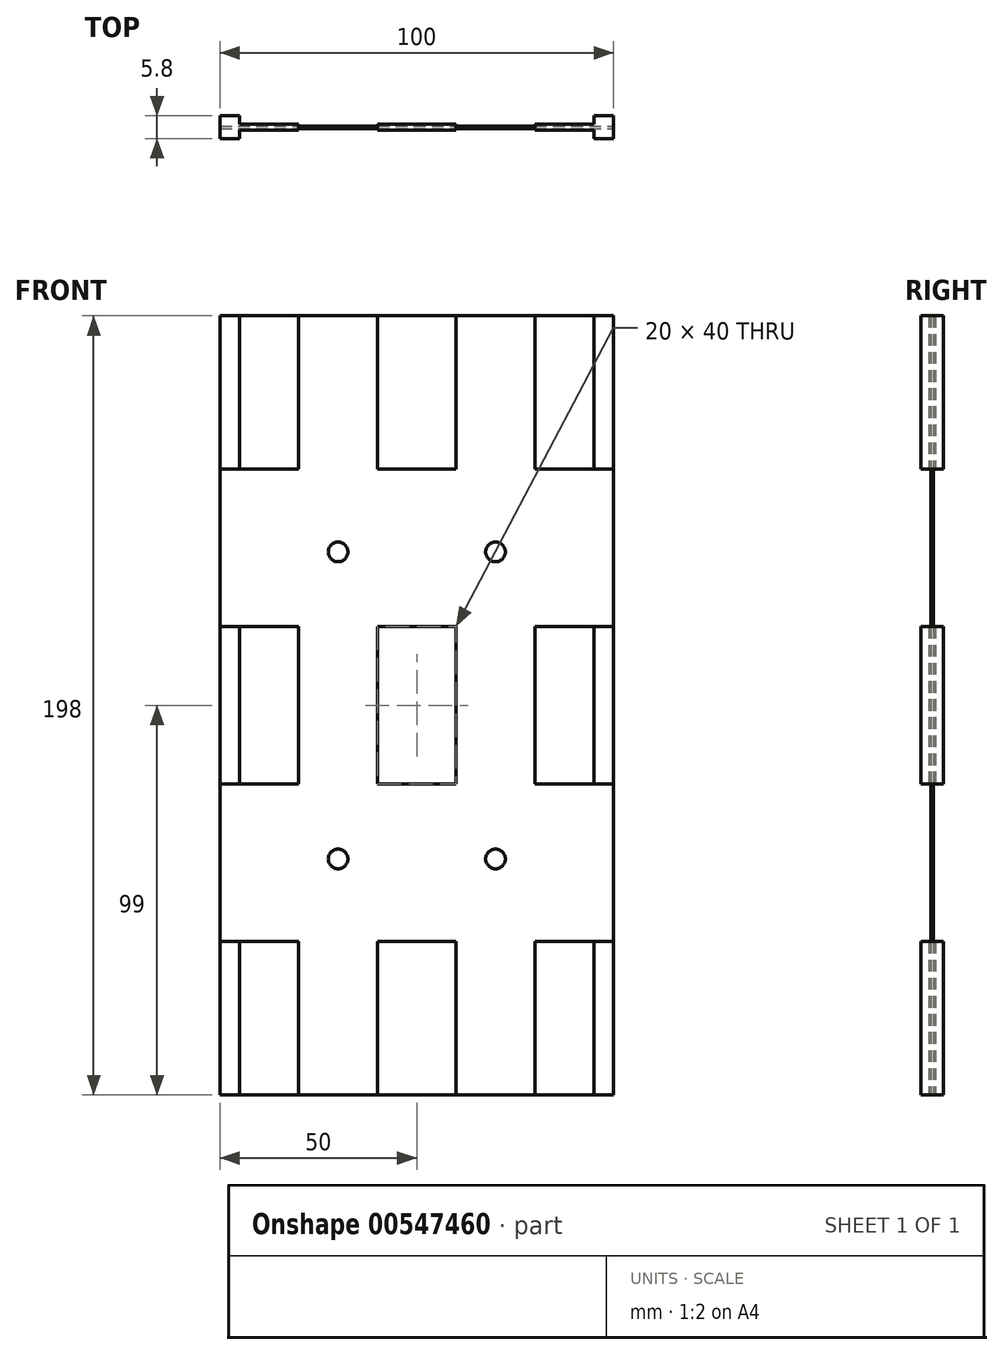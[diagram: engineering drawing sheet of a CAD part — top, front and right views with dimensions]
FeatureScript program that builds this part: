
annotation { "Feature Type Name" : "Feature", "Feature Type Description" : "" }
export const myFeature = defineFeature(function(context is Context, id is Id, definition is map)
    precondition{}
    {
        {
            var Q0;
            Q0=qCreatedBy(makeId("Front.planeOp"),FACE);
            var sketch = newSketch(context, id + "F0", { "sketchPlane" : qUnion([Q0])});
            skLineSegment(sketch, "E0.bottom", {"start": v(50, -99) * mm, "end": v(-50, -99) * mm});
            skLineSegment(sketch, "E0.top", {"start": v(50, 99) * mm, "end": v(-50, 99) * mm});
            skLineSegment(sketch, "E0.left", {"start": v(50, -99) * mm, "end": v(50, 99) * mm});
            skLineSegment(sketch, "E0.right", {"start": v(-50, -99) * mm, "end": v(-50, 99) * mm});
            skPoint(sketch, "E0.middle", {"position": v(0, 0) * mm});
            skLineSegment(sketch, "E1", {"start": v(45, 99) * mm, "end": v(45, -99) * mm});
            skLineSegment(sketch, "E2", {"start": v(30, 99) * mm, "end": v(30, -99) * mm});
            skLineSegment(sketch, "E3", {"start": v(10, 99) * mm, "end": v(10, -99) * mm});
            skLineSegment(sketch, "E4", {"start": v(-10, 99) * mm, "end": v(-10, -99) * mm});
            skLineSegment(sketch, "E5", {"start": v(-30, 99) * mm, "end": v(-30, -99) * mm});
            skLineSegment(sketch, "E6", {"start": v(-45, 99) * mm, "end": v(-45, -99) * mm});
            skLineSegment(sketch, "E7", {"start": v(-50, 60) * mm, "end": v(50, 60) * mm});
            skLineSegment(sketch, "E8", {"start": v(-50, 20) * mm, "end": v(50, 20) * mm});
            skLineSegment(sketch, "E9", {"start": v(-50, -20) * mm, "end": v(50, -20) * mm});
            skLineSegment(sketch, "E10", {"start": v(-50, -60) * mm, "end": v(50, -60) * mm});
            skSolve(sketch);
        }
        {
            var Q0;
            {var subQ0=sQuery(id+"F0.wireOp",EDGE,"E0.right");var subQ1=sQuery(id+"F0.wireOp",EDGE,"E0.bottom");var subQ2=makeQuery(id+"F0.imprint","INTERSECT",VERTEX,{"derivedFrom":[subQ1,subQ0]});Q0=makeQuery(id+"F0.imprint","IMPRINT",FACE,{"disambiguationData":[TD([[makeQuery(id+"F0.imprint","IMPRINT",EDGE,{"disambiguationData":[TD([[subQ2,1.0]])],"derivedFrom":subQ1}),-1.0]])]});}
            var Q1;
            {var subQ0=sQuery(id+"F0.wireOp",EDGE,"E0.right");var subQ1=sQuery(id+"F0.wireOp",EDGE,"E0.top");var subQ2=makeQuery(id+"F0.imprint","INTERSECT",VERTEX,{"derivedFrom":[subQ1,subQ0]});Q1=makeQuery(id+"F0.imprint","IMPRINT",FACE,{"disambiguationData":[TD([[makeQuery(id+"F0.imprint","IMPRINT",EDGE,{"disambiguationData":[TD([[subQ2,1.0]])],"derivedFrom":subQ1}),1.0]])]});}
            var Q2;
            {var subQ0=sQuery(id+"F0.wireOp",EDGE,"E8");var subQ1=sQuery(id+"F0.wireOp",EDGE,"E0.right");var subQ2=makeQuery(id+"F0.imprint","INTERSECT",VERTEX,{"derivedFrom":[subQ1,subQ0]});Q2=makeQuery(id+"F0.imprint","IMPRINT",FACE,{"disambiguationData":[TD([[makeQuery(id+"F0.imprint","IMPRINT",EDGE,{"disambiguationData":[TD([[subQ2,1.0]])],"derivedFrom":subQ1}),-1.0]])]});}
            var Q3;
            {var subQ0=sQuery(id+"F0.wireOp",EDGE,"E0.left");var subQ1=sQuery(id+"F0.wireOp",EDGE,"E0.bottom");var subQ2=makeQuery(id+"F0.imprint","INTERSECT",VERTEX,{"derivedFrom":[subQ1,subQ0]});Q3=makeQuery(id+"F0.imprint","IMPRINT",FACE,{"disambiguationData":[TD([[makeQuery(id+"F0.imprint","IMPRINT",EDGE,{"disambiguationData":[TD([[subQ2,-1.0]])],"derivedFrom":subQ1}),-1.0]])]});}
            var Q4;
            {var subQ0=sQuery(id+"F0.wireOp",EDGE,"E0.left");var subQ1=sQuery(id+"F0.wireOp",EDGE,"E0.top");var subQ2=makeQuery(id+"F0.imprint","INTERSECT",VERTEX,{"derivedFrom":[subQ1,subQ0]});Q4=makeQuery(id+"F0.imprint","IMPRINT",FACE,{"disambiguationData":[TD([[makeQuery(id+"F0.imprint","IMPRINT",EDGE,{"disambiguationData":[TD([[subQ2,-1.0]])],"derivedFrom":subQ1}),1.0]])]});}
            var Q5;
            {var subQ0=sQuery(id+"F0.wireOp",EDGE,"E8");var subQ1=sQuery(id+"F0.wireOp",EDGE,"E0.left");var subQ2=makeQuery(id+"F0.imprint","INTERSECT",VERTEX,{"derivedFrom":[subQ1,subQ0]});Q5=makeQuery(id+"F0.imprint","IMPRINT",FACE,{"disambiguationData":[TD([[makeQuery(id+"F0.imprint","IMPRINT",EDGE,{"disambiguationData":[TD([[subQ2,1.0]])],"derivedFrom":subQ1}),1.0]])]});}
            extrude(context, id + "F1", {"entities" : qUnion([Q0, Q1, Q2, Q3, Q4, Q5]), "endBound" : BoundingType.SYMMETRIC, "depth" : 5.8 * mm, "offsetDistance" : 25 * mm});
        }
        {
            var Q0;
            {var subQ0=sQuery(id+"F0.wireOp",EDGE,"E5");var subQ1=sQuery(id+"F0.wireOp",EDGE,"E0.bottom");var subQ2=makeQuery(id+"F0.imprint","INTERSECT",VERTEX,{"derivedFrom":[subQ1,subQ0]});Q0=makeQuery(id+"F0.imprint","IMPRINT",FACE,{"disambiguationData":[TD([[makeQuery(id+"F0.imprint","IMPRINT",EDGE,{"disambiguationData":[TD([[subQ2,-1.0]])],"derivedFrom":subQ1}),-1.0]])]});}
            var Q1;
            {var subQ0=sQuery(id+"F0.wireOp",EDGE,"E5");var subQ1=sQuery(id+"F0.wireOp",EDGE,"E0.top");var subQ2=makeQuery(id+"F0.imprint","INTERSECT",VERTEX,{"derivedFrom":[subQ1,subQ0]});Q1=makeQuery(id+"F0.imprint","IMPRINT",FACE,{"disambiguationData":[TD([[makeQuery(id+"F0.imprint","IMPRINT",EDGE,{"disambiguationData":[TD([[subQ2,-1.0]])],"derivedFrom":subQ1}),1.0]])]});}
            var Q2;
            {var subQ0=sQuery(id+"F0.wireOp",EDGE,"E8");var subQ1=sQuery(id+"F0.wireOp",EDGE,"E5");var subQ2=makeQuery(id+"F0.imprint","INTERSECT",VERTEX,{"derivedFrom":[subQ1,subQ0]});Q2=makeQuery(id+"F0.imprint","IMPRINT",FACE,{"disambiguationData":[TD([[makeQuery(id+"F0.imprint","IMPRINT",EDGE,{"disambiguationData":[TD([[subQ2,-1.0]])],"derivedFrom":subQ1}),-1.0]])]});}
            var Q3;
            {var subQ0=sQuery(id+"F0.wireOp",EDGE,"E1");var subQ1=sQuery(id+"F0.wireOp",EDGE,"E0.bottom");var subQ2=makeQuery(id+"F0.imprint","INTERSECT",VERTEX,{"derivedFrom":[subQ1,subQ0]});Q3=makeQuery(id+"F0.imprint","IMPRINT",FACE,{"disambiguationData":[TD([[makeQuery(id+"F0.imprint","IMPRINT",EDGE,{"disambiguationData":[TD([[subQ2,-1.0]])],"derivedFrom":subQ1}),-1.0]])]});}
            var Q4;
            {var subQ0=sQuery(id+"F0.wireOp",EDGE,"E1");var subQ1=sQuery(id+"F0.wireOp",EDGE,"E0.top");var subQ2=makeQuery(id+"F0.imprint","INTERSECT",VERTEX,{"derivedFrom":[subQ1,subQ0]});Q4=makeQuery(id+"F0.imprint","IMPRINT",FACE,{"disambiguationData":[TD([[makeQuery(id+"F0.imprint","IMPRINT",EDGE,{"disambiguationData":[TD([[subQ2,-1.0]])],"derivedFrom":subQ1}),1.0]])]});}
            var Q5;
            {var subQ0=sQuery(id+"F0.wireOp",EDGE,"E8");var subQ1=sQuery(id+"F0.wireOp",EDGE,"E1");var subQ2=makeQuery(id+"F0.imprint","INTERSECT",VERTEX,{"derivedFrom":[subQ1,subQ0]});Q5=makeQuery(id+"F0.imprint","IMPRINT",FACE,{"disambiguationData":[TD([[makeQuery(id+"F0.imprint","IMPRINT",EDGE,{"disambiguationData":[TD([[subQ2,-1.0]])],"derivedFrom":subQ1}),-1.0]])]});}
            var Q6;
            {var subQ0=sQuery(id+"F0.wireOp",EDGE,"E3");var subQ1=sQuery(id+"F0.wireOp",EDGE,"E0.bottom");var subQ2=makeQuery(id+"F0.imprint","INTERSECT",VERTEX,{"derivedFrom":[subQ1,subQ0]});Q6=makeQuery(id+"F0.imprint","IMPRINT",FACE,{"disambiguationData":[TD([[makeQuery(id+"F0.imprint","IMPRINT",EDGE,{"disambiguationData":[TD([[subQ2,-1.0]])],"derivedFrom":subQ1}),-1.0]])]});}
            var Q7;
            {var subQ0=sQuery(id+"F0.wireOp",EDGE,"E3");var subQ1=sQuery(id+"F0.wireOp",EDGE,"E0.top");var subQ2=makeQuery(id+"F0.imprint","INTERSECT",VERTEX,{"derivedFrom":[subQ1,subQ0]});Q7=makeQuery(id+"F0.imprint","IMPRINT",FACE,{"disambiguationData":[TD([[makeQuery(id+"F0.imprint","IMPRINT",EDGE,{"disambiguationData":[TD([[subQ2,-1.0]])],"derivedFrom":subQ1}),1.0]])]});}
            var Q8;
            {var subQ0=sQuery(id+"F0.wireOp",EDGE,"E8");var subQ1=sQuery(id+"F0.wireOp",EDGE,"E3");var subQ2=makeQuery(id+"F0.imprint","INTERSECT",VERTEX,{"derivedFrom":[subQ1,subQ0]});Q8=makeQuery(id+"F0.imprint","IMPRINT",FACE,{"disambiguationData":[TD([[makeQuery(id+"F0.imprint","IMPRINT",EDGE,{"disambiguationData":[TD([[subQ2,-1.0]])],"derivedFrom":subQ1}),-1.0]])]});}
            var Q9;
            {var subQ0=sQuery(id+"F0.wireOp",EDGE,"E0.right");var subQ1=sQuery(id+"F0.wireOp",EDGE,"E0.bottom");var subQ2=makeQuery(id+"F0.imprint","INTERSECT",VERTEX,{"derivedFrom":[subQ1,subQ0]});Q9=makeQuery(id+"F0.imprint","IMPRINT",FACE,{"disambiguationData":[TD([[makeQuery(id+"F0.imprint","IMPRINT",EDGE,{"disambiguationData":[TD([[subQ2,1.0]])],"derivedFrom":subQ1}),-1.0]])]});}
            var Q10;
            {var subQ0=sQuery(id+"F0.wireOp",EDGE,"E0.right");var subQ1=sQuery(id+"F0.wireOp",EDGE,"E0.top");var subQ2=makeQuery(id+"F0.imprint","INTERSECT",VERTEX,{"derivedFrom":[subQ1,subQ0]});Q10=makeQuery(id+"F0.imprint","IMPRINT",FACE,{"disambiguationData":[TD([[makeQuery(id+"F0.imprint","IMPRINT",EDGE,{"disambiguationData":[TD([[subQ2,1.0]])],"derivedFrom":subQ1}),1.0]])]});}
            var Q11;
            {var subQ0=sQuery(id+"F0.wireOp",EDGE,"E8");var subQ1=sQuery(id+"F0.wireOp",EDGE,"E0.right");var subQ2=makeQuery(id+"F0.imprint","INTERSECT",VERTEX,{"derivedFrom":[subQ1,subQ0]});Q11=makeQuery(id+"F0.imprint","IMPRINT",FACE,{"disambiguationData":[TD([[makeQuery(id+"F0.imprint","IMPRINT",EDGE,{"disambiguationData":[TD([[subQ2,1.0]])],"derivedFrom":subQ1}),-1.0]])]});}
            extrude(context, id + "F2", {"entities" : qUnion([Q0, Q1, Q2, Q3, Q4, Q5, Q6, Q7, Q8, Q9, Q10, Q11]), "operationType" : NewBodyOperationType.ADD, "endBound" : BoundingType.SYMMETRIC, "depth" : 1.6 * mm, "offsetDistance" : 25 * mm});
        }
        {
            var Q0;
            {var subQ0=sQuery(id+"F0.wireOp",EDGE,"E4");Q0=makeQuery(id+"F0.imprint","IMPRINT",FACE,{"disambiguationData":[TD([[makeQuery(id+"F0.imprint","IMPRINT",EDGE,{"derivedFrom":subQ0}),-1.0]])]});}
            var Q1;
            {var subQ0=sQuery(id+"F0.wireOp",EDGE,"E2");Q1=makeQuery(id+"F0.imprint","IMPRINT",FACE,{"disambiguationData":[TD([[makeQuery(id+"F0.imprint","IMPRINT",EDGE,{"derivedFrom":subQ0}),-1.0]])]});}
            var Q2;
            {var subQ0=sQuery(id+"F0.wireOp",EDGE,"E7");var subQ1=sQuery(id+"F0.wireOp",EDGE,"E0.right");var subQ2=makeQuery(id+"F0.imprint","INTERSECT",VERTEX,{"derivedFrom":[subQ1,subQ0]});Q2=makeQuery(id+"F0.imprint","IMPRINT",FACE,{"disambiguationData":[TD([[makeQuery(id+"F0.imprint","IMPRINT",EDGE,{"disambiguationData":[TD([[subQ2,1.0]])],"derivedFrom":subQ1}),-1.0]])]});}
            var Q3;
            {var subQ0=sQuery(id+"F0.wireOp",EDGE,"E7");var subQ1=sQuery(id+"F0.wireOp",EDGE,"E5");var subQ2=makeQuery(id+"F0.imprint","INTERSECT",VERTEX,{"derivedFrom":[subQ1,subQ0]});Q3=makeQuery(id+"F0.imprint","IMPRINT",FACE,{"disambiguationData":[TD([[makeQuery(id+"F0.imprint","IMPRINT",EDGE,{"disambiguationData":[TD([[subQ2,-1.0]])],"derivedFrom":subQ1}),-1.0]])]});}
            var Q4;
            {var subQ0=sQuery(id+"F0.wireOp",EDGE,"E7");var subQ1=sQuery(id+"F0.wireOp",EDGE,"E3");var subQ2=makeQuery(id+"F0.imprint","INTERSECT",VERTEX,{"derivedFrom":[subQ1,subQ0]});Q4=makeQuery(id+"F0.imprint","IMPRINT",FACE,{"disambiguationData":[TD([[makeQuery(id+"F0.imprint","IMPRINT",EDGE,{"disambiguationData":[TD([[subQ2,-1.0]])],"derivedFrom":subQ1}),-1.0]])]});}
            var Q5;
            {var subQ0=sQuery(id+"F0.wireOp",EDGE,"E7");var subQ1=sQuery(id+"F0.wireOp",EDGE,"E1");var subQ2=makeQuery(id+"F0.imprint","INTERSECT",VERTEX,{"derivedFrom":[subQ1,subQ0]});Q5=makeQuery(id+"F0.imprint","IMPRINT",FACE,{"disambiguationData":[TD([[makeQuery(id+"F0.imprint","IMPRINT",EDGE,{"disambiguationData":[TD([[subQ2,-1.0]])],"derivedFrom":subQ1}),-1.0]])]});}
            var Q6;
            {var subQ0=sQuery(id+"F0.wireOp",EDGE,"E7");var subQ1=sQuery(id+"F0.wireOp",EDGE,"E0.left");var subQ2=makeQuery(id+"F0.imprint","INTERSECT",VERTEX,{"derivedFrom":[subQ1,subQ0]});Q6=makeQuery(id+"F0.imprint","IMPRINT",FACE,{"disambiguationData":[TD([[makeQuery(id+"F0.imprint","IMPRINT",EDGE,{"disambiguationData":[TD([[subQ2,1.0]])],"derivedFrom":subQ1}),1.0]])]});}
            var Q7;
            {var subQ0=sQuery(id+"F0.wireOp",EDGE,"E9");var subQ1=sQuery(id+"F0.wireOp",EDGE,"E0.left");var subQ2=makeQuery(id+"F0.imprint","INTERSECT",VERTEX,{"derivedFrom":[subQ1,subQ0]});Q7=makeQuery(id+"F0.imprint","IMPRINT",FACE,{"disambiguationData":[TD([[makeQuery(id+"F0.imprint","IMPRINT",EDGE,{"disambiguationData":[TD([[subQ2,1.0]])],"derivedFrom":subQ1}),1.0]])]});}
            var Q8;
            {var subQ0=sQuery(id+"F0.wireOp",EDGE,"E9");var subQ1=sQuery(id+"F0.wireOp",EDGE,"E1");var subQ2=makeQuery(id+"F0.imprint","INTERSECT",VERTEX,{"derivedFrom":[subQ1,subQ0]});Q8=makeQuery(id+"F0.imprint","IMPRINT",FACE,{"disambiguationData":[TD([[makeQuery(id+"F0.imprint","IMPRINT",EDGE,{"disambiguationData":[TD([[subQ2,-1.0]])],"derivedFrom":subQ1}),-1.0]])]});}
            var Q9;
            {var subQ0=sQuery(id+"F0.wireOp",EDGE,"E9");var subQ1=sQuery(id+"F0.wireOp",EDGE,"E3");var subQ2=makeQuery(id+"F0.imprint","INTERSECT",VERTEX,{"derivedFrom":[subQ1,subQ0]});Q9=makeQuery(id+"F0.imprint","IMPRINT",FACE,{"disambiguationData":[TD([[makeQuery(id+"F0.imprint","IMPRINT",EDGE,{"disambiguationData":[TD([[subQ2,-1.0]])],"derivedFrom":subQ1}),-1.0]])]});}
            var Q10;
            {var subQ0=sQuery(id+"F0.wireOp",EDGE,"E9");var subQ1=sQuery(id+"F0.wireOp",EDGE,"E5");var subQ2=makeQuery(id+"F0.imprint","INTERSECT",VERTEX,{"derivedFrom":[subQ1,subQ0]});Q10=makeQuery(id+"F0.imprint","IMPRINT",FACE,{"disambiguationData":[TD([[makeQuery(id+"F0.imprint","IMPRINT",EDGE,{"disambiguationData":[TD([[subQ2,-1.0]])],"derivedFrom":subQ1}),-1.0]])]});}
            var Q11;
            {var subQ0=sQuery(id+"F0.wireOp",EDGE,"E9");var subQ1=sQuery(id+"F0.wireOp",EDGE,"E0.right");var subQ2=makeQuery(id+"F0.imprint","INTERSECT",VERTEX,{"derivedFrom":[subQ1,subQ0]});Q11=makeQuery(id+"F0.imprint","IMPRINT",FACE,{"disambiguationData":[TD([[makeQuery(id+"F0.imprint","IMPRINT",EDGE,{"disambiguationData":[TD([[subQ2,1.0]])],"derivedFrom":subQ1}),-1.0]])]});}
            extrude(context, id + "F3", {"entities" : qUnion([Q0, Q1, Q2, Q3, Q4, Q5, Q6, Q7, Q8, Q9, Q10, Q11]), "endBound" : BoundingType.SYMMETRIC, "depth" : 0.6 * mm, "offsetDistance" : 25 * mm});
        }
        {
            var Q0;
            Q0=makeQuery(id+"F3.opExtrude","CAP_FACE",FACE,{"disambiguationData":[OSD([sQuery(id+"F0.wireOp",EDGE,"E0.bottom"),sQuery(id+"F0.wireOp",EDGE,"E0.top"),sQuery(id+"F0.wireOp",EDGE,"E0.left"),sQuery(id+"F0.wireOp",EDGE,"E0.right"),sQuery(id+"F0.wireOp",EDGE,"E2"),sQuery(id+"F0.wireOp",EDGE,"E3"),sQuery(id+"F0.wireOp",EDGE,"E4"),sQuery(id+"F0.wireOp",EDGE,"E5"),sQuery(id+"F0.wireOp",EDGE,"E7"),sQuery(id+"F0.wireOp",EDGE,"E8"),sQuery(id+"F0.wireOp",EDGE,"E9"),sQuery(id+"F0.wireOp",EDGE,"E10")])],"isStart":false});
            var sketch = newSketch(context, id + "F4", { "sketchPlane" : qUnion([Q0])});
            skCircle(sketch, "E11", {"center": v(-20, 39) * mm, "radius": 2.5 * mm});
            skCircle(sketch, "E12", {"center": v(20, 39) * mm, "radius": 2.5 * mm});
            skCircle(sketch, "E13", {"center": v(-20, -39) * mm, "radius": 2.5 * mm});
            skCircle(sketch, "E14", {"center": v(20, -39) * mm, "radius": 2.5 * mm});
            skSolve(sketch);
        }
        {
            var Q0;
            Q0=makeQuery(id+"F4.imprint","IMPRINT",FACE,{"disambiguationData":[TD([[makeQuery(id+"F4.imprint","IMPRINT",EDGE,{"derivedFrom":sQuery(id+"F4.wireOp",EDGE,"E11")}),1.0]])]});
            var Q1;
            Q1=makeQuery(id+"F4.imprint","IMPRINT",FACE,{"disambiguationData":[TD([[makeQuery(id+"F4.imprint","IMPRINT",EDGE,{"derivedFrom":sQuery(id+"F4.wireOp",EDGE,"E12")}),1.0]])]});
            var Q2;
            Q2=makeQuery(id+"F4.imprint","IMPRINT",FACE,{"disambiguationData":[TD([[makeQuery(id+"F4.imprint","IMPRINT",EDGE,{"derivedFrom":sQuery(id+"F4.wireOp",EDGE,"E13")}),1.0]])]});
            var Q3;
            Q3=makeQuery(id+"F4.imprint","IMPRINT",FACE,{"disambiguationData":[TD([[makeQuery(id+"F4.imprint","IMPRINT",EDGE,{"derivedFrom":sQuery(id+"F4.wireOp",EDGE,"E14")}),1.0]])]});
            extrude(context, id + "F5", {"entities" : qUnion([Q0, Q1, Q2, Q3]), "operationType" : NewBodyOperationType.REMOVE, "endBound" : BoundingType.THROUGH_ALL, "oppositeDirection" : true, "depth" : 25 * mm, "offsetDistance" : 25 * mm});
        }
    });
